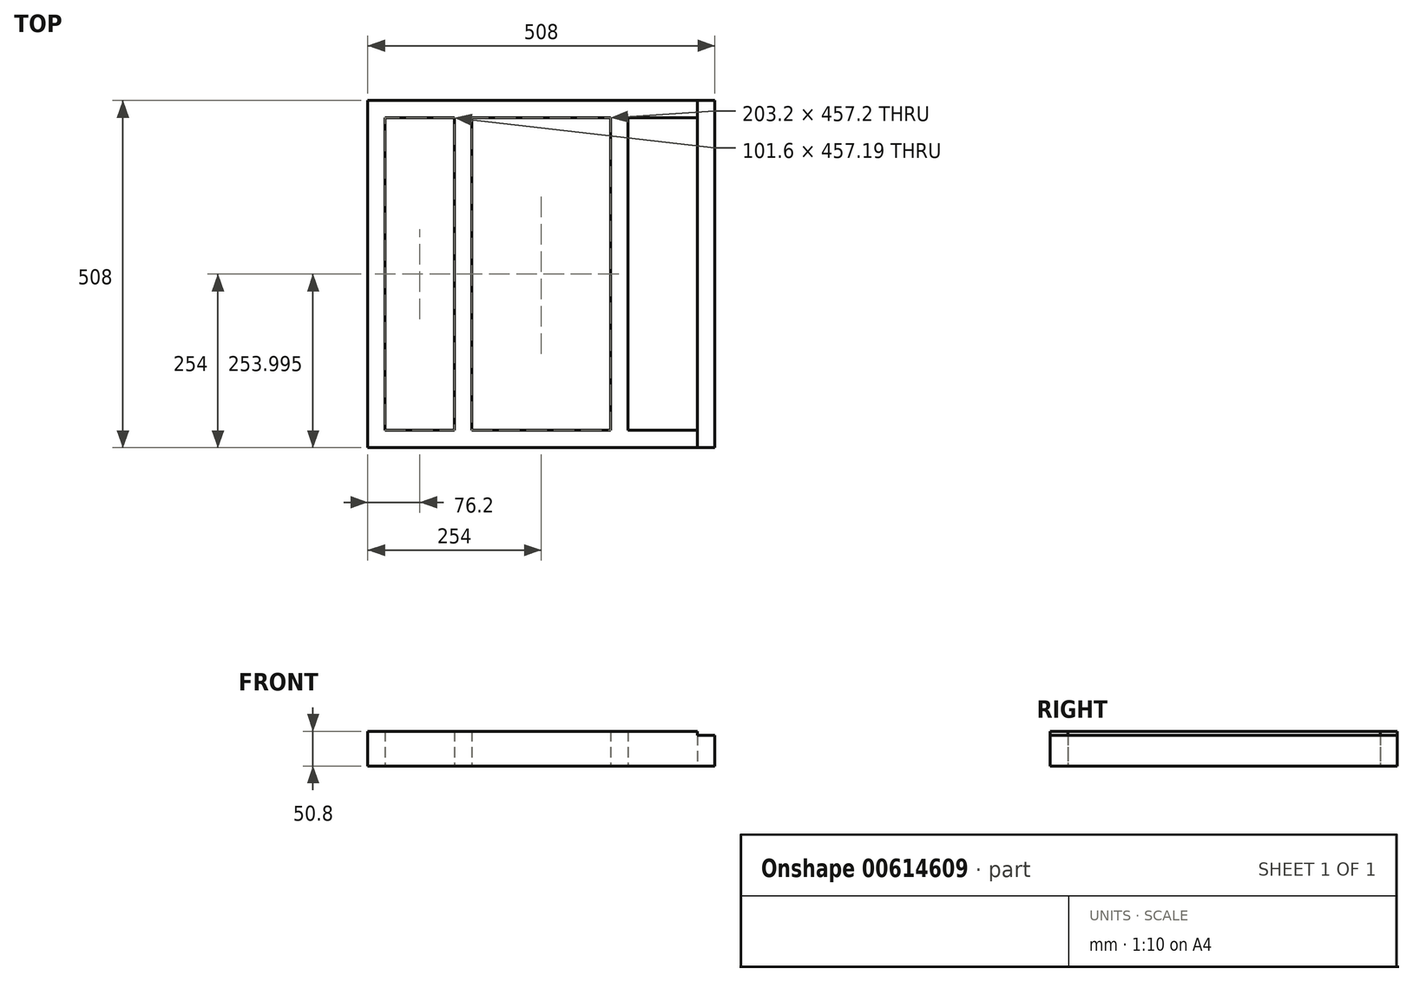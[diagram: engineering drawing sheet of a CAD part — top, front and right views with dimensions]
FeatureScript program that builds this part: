
annotation { "Feature Type Name" : "Feature", "Feature Type Description" : "" }
export const myFeature = defineFeature(function(context is Context, id is Id, definition is map)
    precondition{}
    {
        {
            var Q0;
            Q0=qCreatedBy(makeId("Top.planeOp"),FACE);
            var sketch = newSketch(context, id + "F0", { "sketchPlane" : qUnion([Q0])});
            skLineSegment(sketch, "E0.bottom", {"start": v(-254, 213.59) * mm, "end": v(-101.6, 213.59) * mm});
            skLineSegment(sketch, "E0.top", {"start": v(-254, -294.41) * mm, "end": v(-101.6, -294.41) * mm});
            skLineSegment(sketch, "E0.left", {"start": v(-254, 213.59) * mm, "end": v(-254, -294.41) * mm});
            skLineSegment(sketch, "E0.right", {"start": v(-101.6, 188.19) * mm, "end": v(-101.6, -294.41) * mm});
            skLineSegment(sketch, "E1.MirrorCS", {"start": v(101.6, 188.19) * mm, "end": v(101.6, -294.41) * mm});
            skLineSegment(sketch, "E2.MirrorCS", {"start": v(254, 213.59) * mm, "end": v(254, -294.41) * mm});
            skLineSegment(sketch, "E3.MirrorCS", {"start": v(254, 213.59) * mm, "end": v(101.6, 213.59) * mm});
            skLineSegment(sketch, "E4.MirrorCS", {"start": v(254, -294.41) * mm, "end": v(101.6, -294.41) * mm});
            skLineSegment(sketch, "E5.bottom", {"start": v(-101.6, 213.59) * mm, "end": v(101.6, 213.59) * mm});
            skLineSegment(sketch, "E5.top", {"start": v(-101.6, 188.19) * mm, "end": v(101.6, 188.19) * mm});
            skLineSegment(sketch, "E6.bottom", {"start": v(-101.6, -294.41) * mm, "end": v(101.6, -294.41) * mm});
            skLineSegment(sketch, "E6.top", {"start": v(-101.6, -269.01) * mm, "end": v(101.6, -269.01) * mm});
            skLineSegment(sketch, "E6.left", {"start": v(-101.6, -294.41) * mm, "end": v(-101.6, -269.01) * mm});
            skLineSegment(sketch, "E6.right", {"start": v(101.6, -294.41) * mm, "end": v(101.6, -269.01) * mm});
            skLineSegment(sketch, "E7.bottom", {"start": v(-254, 213.59) * mm, "end": v(-228.6, 213.59) * mm});
            skLineSegment(sketch, "E7.top", {"start": v(-254, -294.41) * mm, "end": v(-228.6, -294.41) * mm});
            skLineSegment(sketch, "E7.right", {"start": v(-228.6, 188.18) * mm, "end": v(-228.6, -269.01) * mm});
            skLineSegment(sketch, "E8.MirrorCS", {"start": v(-254, -213.59) * mm, "end": v(-254, 213.59) * mm});
            skLineSegment(sketch, "E9.MirrorCS", {"start": v(228.6, 188.18) * mm, "end": v(228.6, -269.01) * mm});
            skLineSegment(sketch, "E10.bottom", {"start": v(-101.6, 213.59) * mm, "end": v(-127, 213.59) * mm});
            skLineSegment(sketch, "E10.right", {"start": v(-127, 188.18) * mm, "end": v(-127, -269.01) * mm});
            skLineSegment(sketch, "E11.MirrorCS", {"start": v(127, 188.18) * mm, "end": v(127, -269.01) * mm});
            skLineSegment(sketch, "E12.MirrorCS", {"start": v(101.6, 188.19) * mm, "end": v(101.6, -269.01) * mm});
            skLineSegment(sketch, "E13.bottom", {"start": v(-101.6, 213.59) * mm, "end": v(-254, 213.59) * mm});
            skLineSegment(sketch, "E13.top", {"start": v(-127, 188.18) * mm, "end": v(-228.6, 188.18) * mm});
            skLineSegment(sketch, "E13.left", {"start": v(-101.6, 188.19) * mm, "end": v(-101.6, 188.18) * mm});
            skLineSegment(sketch, "E13.right", {"start": v(-254, 213.59) * mm, "end": v(-254, 188.18) * mm});
            skLineSegment(sketch, "E14.MirrorCS", {"start": v(127, 188.18) * mm, "end": v(228.6, 188.18) * mm});
            skLineSegment(sketch, "E15.MirrorCS", {"start": v(101.6, 213.59) * mm, "end": v(254, 213.59) * mm});
            skPoint(sketch, "E16.orphan", {"position": v(127, 213.59) * mm});
            skPoint(sketch, "E17.orphan", {"position": v(228.6, 213.59) * mm});
            skLineSegment(sketch, "E18.bottom", {"start": v(-228.6, -294.41) * mm, "end": v(-127, -294.41) * mm});
            skLineSegment(sketch, "E18.top", {"start": v(-228.6, -269.01) * mm, "end": v(-127, -269.01) * mm});
            skLineSegment(sketch, "E19.bottom", {"start": v(127, -269.01) * mm, "end": v(228.6, -269.01) * mm});
            skLineSegment(sketch, "E19.top", {"start": v(101.6, -294.41) * mm, "end": v(254, -294.41) * mm});
            skLineSegment(sketch, "E19.right", {"start": v(254, -269.01) * mm, "end": v(254, -294.41) * mm});
            skPoint(sketch, "E20.orphan", {"position": v(127, -294.41) * mm});
            skPoint(sketch, "E21.orphan", {"position": v(228.6, -294.41) * mm});
            skPoint(sketch, "E22.orphan", {"position": v(101.6, -294.41) * mm});
            skPoint(sketch, "E23.orphan", {"position": v(101.6, 213.59) * mm});
            skPoint(sketch, "E24.orphan", {"position": v(-254, 294.41) * mm});
            skSolve(sketch);
        }
        {
            var Q0;
            Q0 = qSketchRegion(id + "F0", true);
            extrude(context, id + "F1", {"entities" : qUnion([Q0]), "depth" : 50.8 * mm, "offsetDistance" : 25.4 * mm});
        }
        {
            var Q0;
            Q0=makeQuery(id+"F1.opExtrude","CAP_FACE",FACE,{"disambiguationData":[OSD([sQuery(id+"F0.wireOp",EDGE,"E0.top"),sQuery(id+"F0.wireOp",EDGE,"E5.bottom"),sQuery(id+"F0.wireOp",EDGE,"E5.top"),sQuery(id+"F0.wireOp",EDGE,"E6.bottom"),sQuery(id+"F0.wireOp",EDGE,"E6.top"),sQuery(id+"F0.wireOp",EDGE,"E7.top"),sQuery(id+"F0.wireOp",EDGE,"E0.left"),sQuery(id+"F0.wireOp",EDGE,"E7.right"),sQuery(id+"F0.wireOp",EDGE,"E8.MirrorCS"),sQuery(id+"F0.wireOp",EDGE,"E9.MirrorCS"),sQuery(id+"F0.wireOp",EDGE,"E2.MirrorCS"),sQuery(id+"F0.wireOp",EDGE,"E0.right"),sQuery(id+"F0.wireOp",EDGE,"E10.right"),sQuery(id+"F0.wireOp",EDGE,"E11.MirrorCS"),sQuery(id+"F0.wireOp",EDGE,"E12.MirrorCS"),sQuery(id+"F0.wireOp",EDGE,"E13.bottom"),sQuery(id+"F0.wireOp",EDGE,"E13.top"),sQuery(id+"F0.wireOp",EDGE,"E13.left"),sQuery(id+"F0.wireOp",EDGE,"E13.right"),sQuery(id+"F0.wireOp",EDGE,"E14.MirrorCS"),sQuery(id+"F0.wireOp",EDGE,"E15.MirrorCS"),sQuery(id+"F0.wireOp",EDGE,"E18.bottom"),sQuery(id+"F0.wireOp",EDGE,"E18.top"),sQuery(id+"F0.wireOp",EDGE,"E19.bottom"),sQuery(id+"F0.wireOp",EDGE,"E19.top"),sQuery(id+"F0.wireOp",EDGE,"E19.right")])],"isStart":false});
            var Q1;
            Q1=makeQuery(id+"F1.opExtrude","SWEPT_FACE",FACE,{"disambiguationData":[OSD([sQuery(id+"F0.wireOp",EDGE,"E0.left"),sQuery(id+"F0.wireOp",EDGE,"E8.MirrorCS"),sQuery(id+"F0.wireOp",EDGE,"E13.right")])]});
            var Q2;
            Q2=makeQuery(id+"F1.opExtrude","SWEPT_FACE",FACE,{"disambiguationData":[OSD([sQuery(id+"F0.wireOp",EDGE,"E0.top"),sQuery(id+"F0.wireOp",EDGE,"E6.bottom"),sQuery(id+"F0.wireOp",EDGE,"E7.top"),sQuery(id+"F0.wireOp",EDGE,"E18.bottom"),sQuery(id+"F0.wireOp",EDGE,"E19.top")])]});
            var Q3;
            Q3=makeQuery(id+"F1.opExtrude","SWEPT_FACE",FACE,{"disambiguationData":[OSD([sQuery(id+"F0.wireOp",EDGE,"E2.MirrorCS"),sQuery(id+"F0.wireOp",EDGE,"E19.right")])]});
            var Q4;
            Q4=makeQuery(id+"F1.opExtrude","SWEPT_FACE",FACE,{"disambiguationData":[OSD([sQuery(id+"F0.wireOp",EDGE,"E5.bottom"),sQuery(id+"F0.wireOp",EDGE,"E13.bottom"),sQuery(id+"F0.wireOp",EDGE,"E15.MirrorCS")])]});
            var Q5;
            Q5=makeQuery(id+"F1.opExtrude","SWEPT_FACE",FACE,{"disambiguationData":[OSD([sQuery(id+"F0.wireOp",EDGE,"E12.MirrorCS")])]});
            var Q6;
            Q6=makeQuery(id+"F1.opExtrude","SWEPT_FACE",FACE,{"disambiguationData":[OSD([sQuery(id+"F0.wireOp",EDGE,"E9.MirrorCS")])]});
            var Q7;
            Q7=makeQuery(id+"F1.opExtrude","SWEPT_FACE",FACE,{"disambiguationData":[OSD([sQuery(id+"F0.wireOp",EDGE,"E10.right")])]});
            shell(context, id + "F2", {"entities" : qUnion([Q0, Q1, Q2, Q3, Q4, Q5, Q6, Q7]), "thickness" : 45.08 * mm});
        }
    });
